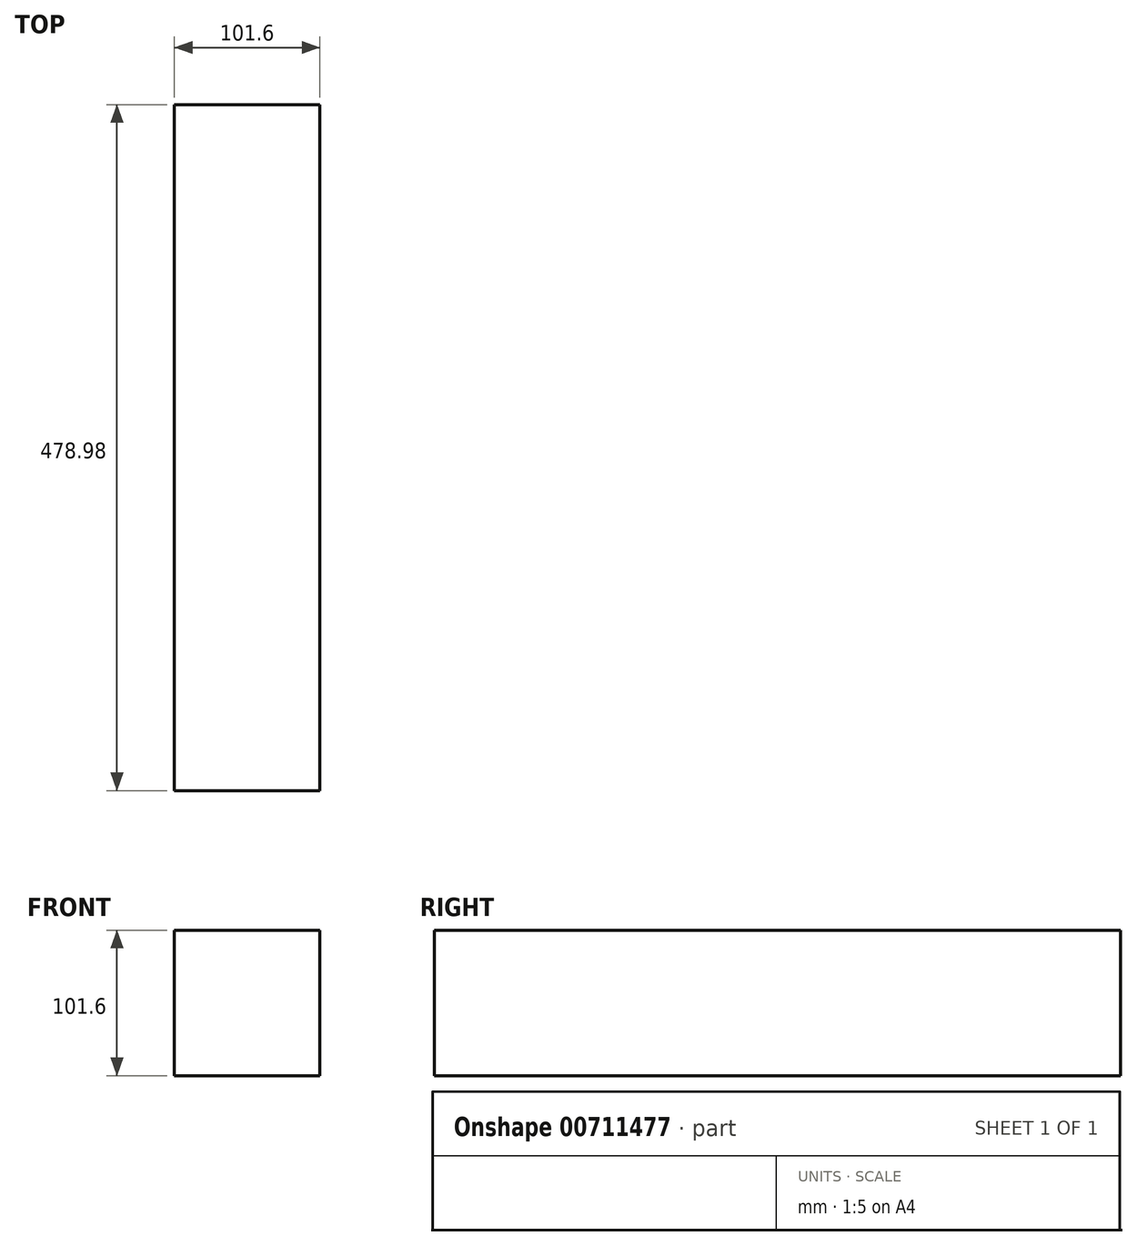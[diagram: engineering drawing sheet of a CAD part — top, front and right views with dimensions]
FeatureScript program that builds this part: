
annotation { "Feature Type Name" : "Feature", "Feature Type Description" : "" }
export const myFeature = defineFeature(function(context is Context, id is Id, definition is map)
    precondition{}
    {
        {
            var Q0;
            Q0=qCreatedBy(makeId("Top.planeOp"),FACE);
            var sketch = newSketch(context, id + "F0", { "sketchPlane" : qUnion([Q0])});
            skLineSegment(sketch, "E0.bottom", {"start": v(-105.95, -211.9) * mm, "end": v(-4.35, -211.9) * mm});
            skLineSegment(sketch, "E0.top", {"start": v(-105.95, 267.08) * mm, "end": v(-4.35, 267.08) * mm});
            skLineSegment(sketch, "E0.left", {"start": v(-105.95, -211.9) * mm, "end": v(-105.95, 267.08) * mm});
            skLineSegment(sketch, "E0.right", {"start": v(-4.35, -211.9) * mm, "end": v(-4.35, 267.08) * mm});
            skSolve(sketch);
        }
        {
            var Q0;
            Q0 = qSketchRegion(id + "F0", true);
            extrude(context, id + "F1", {"entities" : qUnion([Q0]), "depth" : 101.6 * mm, "offsetDistance" : 25.4 * mm});
        }
    });
